# Revit family: Zumtobel TECTON 2 wireless controls
name_source: partatom
category: Lighting Devices
units: mm (PartAtom-declared; Revit-internal decimal feet)

## family parameters
Cut with Voids When Loaded = No
Host = Face
Maintain Annotation Orientation = No
Part Type = Normal
Room Calculation Point = Yes
Round Connector Dimension = Use Diameter
Shared = Yes

## types (6) — shared parameters
Assembly Code = Pr_75_75_27_23
Description = Lighting and occupancy sensors
Export Type to IFC As = IfcSensorType
Luminaire Height = 90 mm
Luminaire Length = 250 mm
Luminaire Width = 60 mm
Manufacturer = Zumtobel Lighting
Type IFC Predefined Type = MOVEMENTSENSOR
zero-valued in all types: Default Elevation

## per-type parameters (varying)
| type | Is HC Type | Is LC/MC Type | Is Only Bluetooth | Material Bluetooth | Material Body | Material Housing | Model | Type Image | URL | Visibility B | Visibility HC | Visibility LC/MC | Visibility NOT HC |
| BC REPEATER TEC2 BK | No | No | Yes | Zumtobel-Plastic-RAL 9003-Signal White | Zumtobel-Plastic-RAL 9005-Jet Black | Zumtobel-Plastic-RAL 9005-Jet Black | 22173111 | ZS_TE2_F_BC_Sensor_BK.jpg | www.zumtobel.com/22173111 | Yes | No | No | Yes |
| BC REPEATER TEC2 WH | No | No | Yes | Zumtobel-Plastic-RAL 9005-Jet Black | Zumtobel-Plastic-RAL 9003-Signal White | Zumtobel-Plastic-RAL 9003-Signal White | 22173073 | ZS_TE2_F_BC_Sensor_WH.jpg | www.zumtobel.com/22173073 | Yes | No | No | Yes |
| DALI MSENS HB BC TEC2 BK | Yes | No | No | Zumtobel-Plastic-RAL 9003-Signal White | Zumtobel-Plastic-RAL 9003-Signal White | Zumtobel-Plastic-RAL 9005-Jet Black | 22173115 | ZS_TEC_F_MSENS_HC_BK.jpg | www.zumtobel.com/22173115 | No | Yes | No | No |
| DALI MSENS HC BC TEC2 WH | Yes | No | No | Zumtobel-Plastic-RAL 9005-Jet Black | Zumtobel-Plastic-RAL 9003-Signal White | Zumtobel-Plastic-RAL 9003-Signal White | 22172959 | ZS_TEC_F_MSENS_HC_WH.jpg | www.zumtobel.com/22172959 | No | Yes | No | No |
| DALI MSENS LC BC TEC2 WH | No | Yes | No | Zumtobel-Plastic-RAL 9005-Jet Black | Zumtobel-Plastic-RAL 9003-Signal White | Zumtobel-Plastic-RAL 9003-Signal White | 22172965 | ZS_TE2_F_MSENS_MC_WH.jpg | www.zumtobel.com/22172965 | No | No | Yes | Yes |
| DALI MSENS LC BC TEC2 BK | No | Yes | No | Zumtobel-Plastic-RAL 9003-Signal White | Zumtobel-Plastic-RAL 9005-Jet Black | Zumtobel-Plastic-RAL 9005-Jet Black | 22173117 | ZS_TE2_F_MSENS_MC_BK.jpg | www.zumtobel.com/22173117 | No | No | Yes | Yes |

## geometry (parser evidence)
native form markers: Sweep x3
no freeform markers — native parametric forms only
